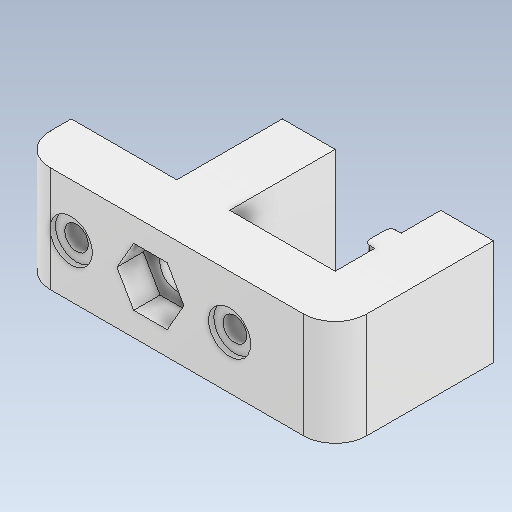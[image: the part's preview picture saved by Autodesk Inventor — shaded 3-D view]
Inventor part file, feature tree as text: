
AUTODESK INVENTOR PART (.ipt)
format: ipt  version: 2020 (Build 240168000, 168)  size: 200,704 bytes
history: native  units: mm
features: extrude x4, sketch x2, other x1, fillet x1
ambient origin geometry x8: Origin, YZ Plane, XZ Plane, XY Plane, X Axis, Y Axis, Z Axis, Center Point
bodies: Body1 (feature_tree)
feature tree (8):
  other  "Bryła1"
  extrude  "Wyciągnięcie proste1"  Depth=20.0mm
  sketch  "Szkic2"
  extrude  "Wyciągnięcie proste2"  Depth=20.0mm
  extrude  "Wyciągnięcie proste3"  Depth=20.0mm
  fillet  "Zaokrąglenie1"  Radius=20.0mm
  extrude  "Wyciągnięcie proste4"  Depth=50.0mm
  sketch  "Szkic1"
